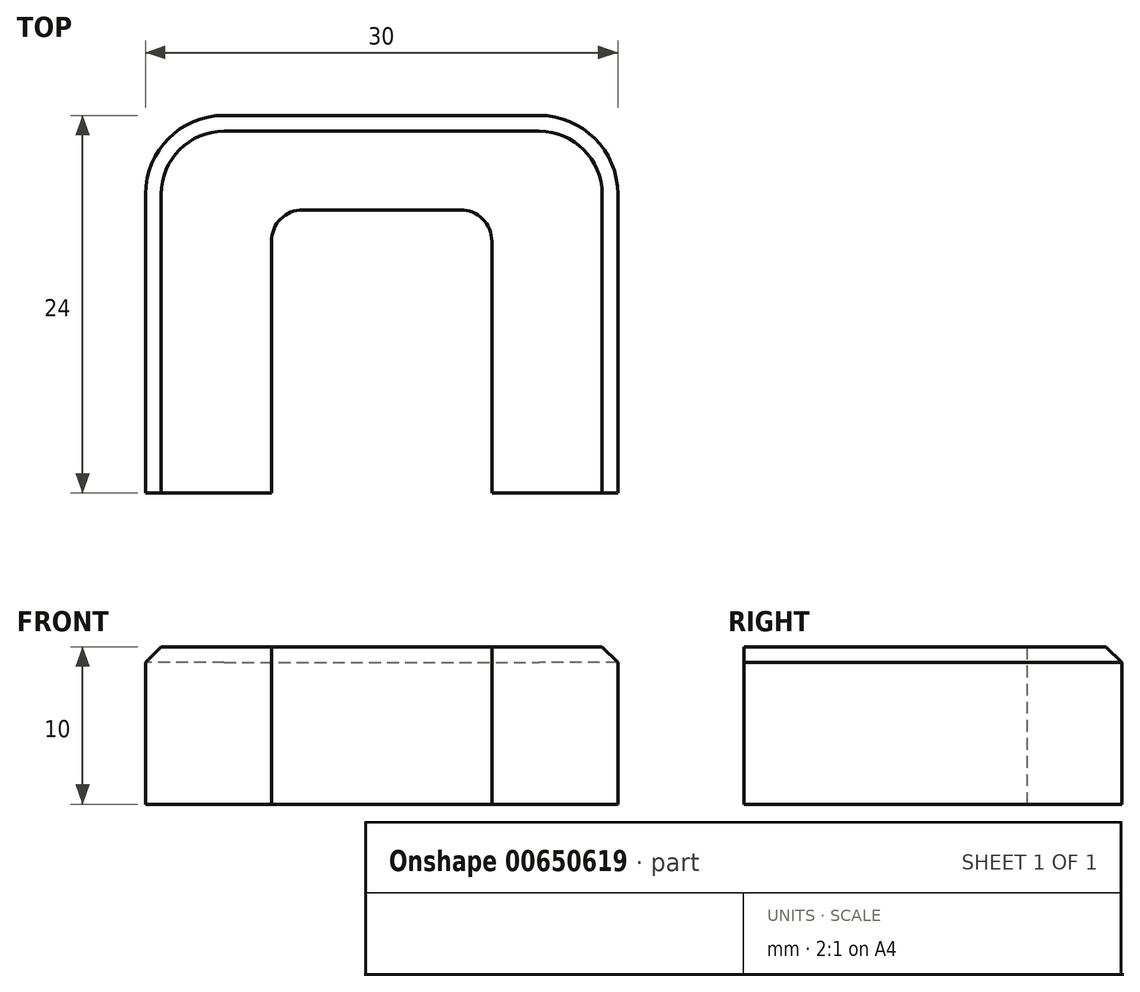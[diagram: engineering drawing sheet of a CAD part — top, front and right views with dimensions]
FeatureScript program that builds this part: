
annotation { "Feature Type Name" : "Feature", "Feature Type Description" : "" }
export const myFeature = defineFeature(function(context is Context, id is Id, definition is map)
    precondition{}
    {
        {
            var Q0;
            Q0=qCreatedBy(makeId("Top.planeOp"),FACE);
            var sketch = newSketch(context, id + "F0", { "sketchPlane" : qUnion([Q0])});
            skLineSegment(sketch, "E0.bottom", {"start": v(-15, 12) * mm, "end": v(15, 12) * mm});
            skLineSegment(sketch, "E0.top", {"start": v(-15, -12) * mm, "end": v(15, -12) * mm});
            skLineSegment(sketch, "E0.left", {"start": v(-15, 12) * mm, "end": v(-15, -12) * mm});
            skLineSegment(sketch, "E0.right", {"start": v(15, 12) * mm, "end": v(15, -12) * mm});
            skPoint(sketch, "E0.middle", {"position": v(0, 0) * mm});
            skSolve(sketch);
        }
        {
            var Q0;
            Q0 = qSketchRegion(id + "F0", true);
            extrude(context, id + "F1", {"entities" : qUnion([Q0]), "depth" : 10 * mm, "offsetDistance" : 25 * mm});
        }
        {
            var Q0;
            Q0=makeQuery(id+"F1.opExtrude","CAP_FACE",FACE,{"disambiguationData":[OSD([sQuery(id+"F0.wireOp",EDGE,"E0.bottom"),sQuery(id+"F0.wireOp",EDGE,"E0.top"),sQuery(id+"F0.wireOp",EDGE,"E0.left"),sQuery(id+"F0.wireOp",EDGE,"E0.right")])],"isStart":false});
            var sketch = newSketch(context, id + "F2", { "sketchPlane" : qUnion([Q0])});
            skLineSegment(sketch, "E1", {"start": v(0, 12) * mm, "end": v(0, -12) * mm, "construction": true});
            skLineSegment(sketch, "E2.bottom", {"start": v(-7, 6) * mm, "end": v(7, 6) * mm});
            skLineSegment(sketch, "E2.top", {"start": v(-7, -12) * mm, "end": v(7, -12) * mm});
            skLineSegment(sketch, "E2.left", {"start": v(-7, 6) * mm, "end": v(-7, -12) * mm});
            skLineSegment(sketch, "E2.right", {"start": v(7, 6) * mm, "end": v(7, -12) * mm});
            skPoint(sketch, "E2.middle", {"position": v(0, -3) * mm});
            skSolve(sketch);
        }
        {
            var Q0;
            Q0 = qSketchRegion(id + "F2", true);
            extrude(context, id + "F3", {"entities" : qUnion([Q0]), "operationType" : NewBodyOperationType.REMOVE, "endBound" : BoundingType.THROUGH_ALL, "oppositeDirection" : true, "depth" : 25 * mm, "offsetDistance" : 25 * mm});
        }
        {
            var Q0;
            Q0=makeQuery(id+"F3.boolean.opBoolean","COPY",EDGE,{"derivedFrom":makeQuery(id+"F3.opExtrude","SWEPT_EDGE",EDGE,{"disambiguationData":[OSD([sQuery(id+"F2.wireOp",EDGE,"E2.bottom"),sQuery(id+"F2.wireOp",EDGE,"E2.left")])]})});
            var Q1;
            Q1=makeQuery(id+"F3.boolean.opBoolean","COPY",EDGE,{"derivedFrom":makeQuery(id+"F3.opExtrude","SWEPT_EDGE",EDGE,{"disambiguationData":[OSD([sQuery(id+"F2.wireOp",EDGE,"E2.bottom"),sQuery(id+"F2.wireOp",EDGE,"E2.right")])]})});
            fillet(context, id + "F4", {"entities" : qUnion([Q0, Q1]), "radius" : 2 * mm, "tangentPropagation" : true, "allowEdgeOverflow" : false});
        }
        {
            var Q0;
            Q0=makeQuery(id+"F1.opExtrude","SWEPT_EDGE",EDGE,{"disambiguationData":[OSD([sQuery(id+"F0.wireOp",EDGE,"E0.bottom"),sQuery(id+"F0.wireOp",EDGE,"E0.left")])]});
            var Q1;
            Q1=makeQuery(id+"F1.opExtrude","SWEPT_EDGE",EDGE,{"disambiguationData":[OSD([sQuery(id+"F0.wireOp",EDGE,"E0.bottom"),sQuery(id+"F0.wireOp",EDGE,"E0.right")])]});
            fillet(context, id + "F5", {"entities" : qUnion([Q0, Q1]), "radius" : 5 * mm, "tangentPropagation" : true, "allowEdgeOverflow" : false});
        }
        {
            var Q0;
            Q0=makeQuery(id+"F1.opExtrude","CAP_EDGE",EDGE,{"disambiguationData":[OSD([sQuery(id+"F0.wireOp",EDGE,"E0.bottom")])],"isStart":false});
            chamfer(context, id + "F6", {"entities" : qUnion([Q0]), "width" : 1 * mm, "tangentPropagation" : true});
        }
    });
